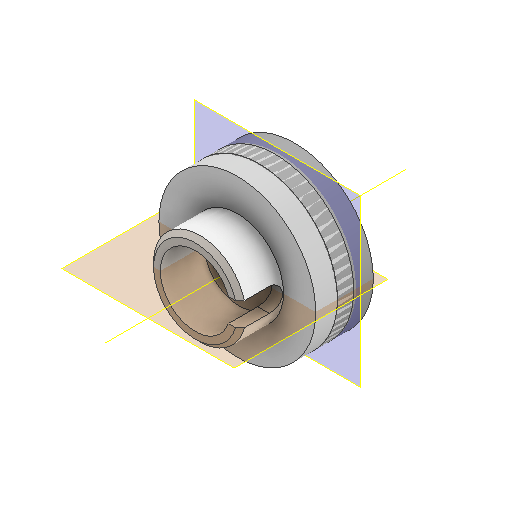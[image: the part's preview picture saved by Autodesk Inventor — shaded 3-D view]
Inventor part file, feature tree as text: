
AUTODESK INVENTOR PART (.ipt)
format: ipt  version: 2022 (Build 260153000, 153)  size: 774,144 bytes
history: native  units: mm
features: other x6, extrude x4, sketch x4, plane x2, projected_geometry x1
ambient origin geometry x8: Origin, YZ Plane, XZ Plane, XY Plane, X Axis, Y Axis, Z Axis, Center Point
bodies: Volumenkörper1 (feature_tree), Volumenkörper2 (feature_tree)
feature tree (17):
  other  "00_SM05FC2-Step.ipt"
  plane  "Arbeitsebene1"
  extrude  "Extrusion1"  [1 undecoded]
  plane  "Arbeitsebene2"
  extrude  "Extrusion2"  Depth=3.0mm TaperAngle=0.0deg
  extrude  "Extrusion3"  Depth=3.0mm
  extrude  "Extrusion4"  [1 undecoded]
  other  "Volumenkörper1::00_SM05FC2-Step.ipt"
  other  "Volumenkörper2::00_SM05FC2-Step.ipt"
  other  "Bezeichnung1"
  sketch  "Skizze1"  dims[d0=10.0mm d1=-0.5mm]
  other  "Arbeitsachse1"
  other  "Arbeitspunkt1"
  sketch  "Skizze3"  dims[d2=3.0mm d3=0.0mm d5=12.12mm d6=0.0mm]
  sketch  "Skizze4"  dims[d7=3.0mm d8=0.3mm d9=0.0mm d10=0.0mm d11=3.0mm]
  sketch  "Skizze5"  dims[d12=0.0mm d13=0.0mm]
  projected_geometry  "Projizierte Kontur1"
note: 2 required parameter values undecoded (feature->parameter linkage not recoverable at this tier; creation-order binding heuristic only, values carry confidence <= 0.55)
